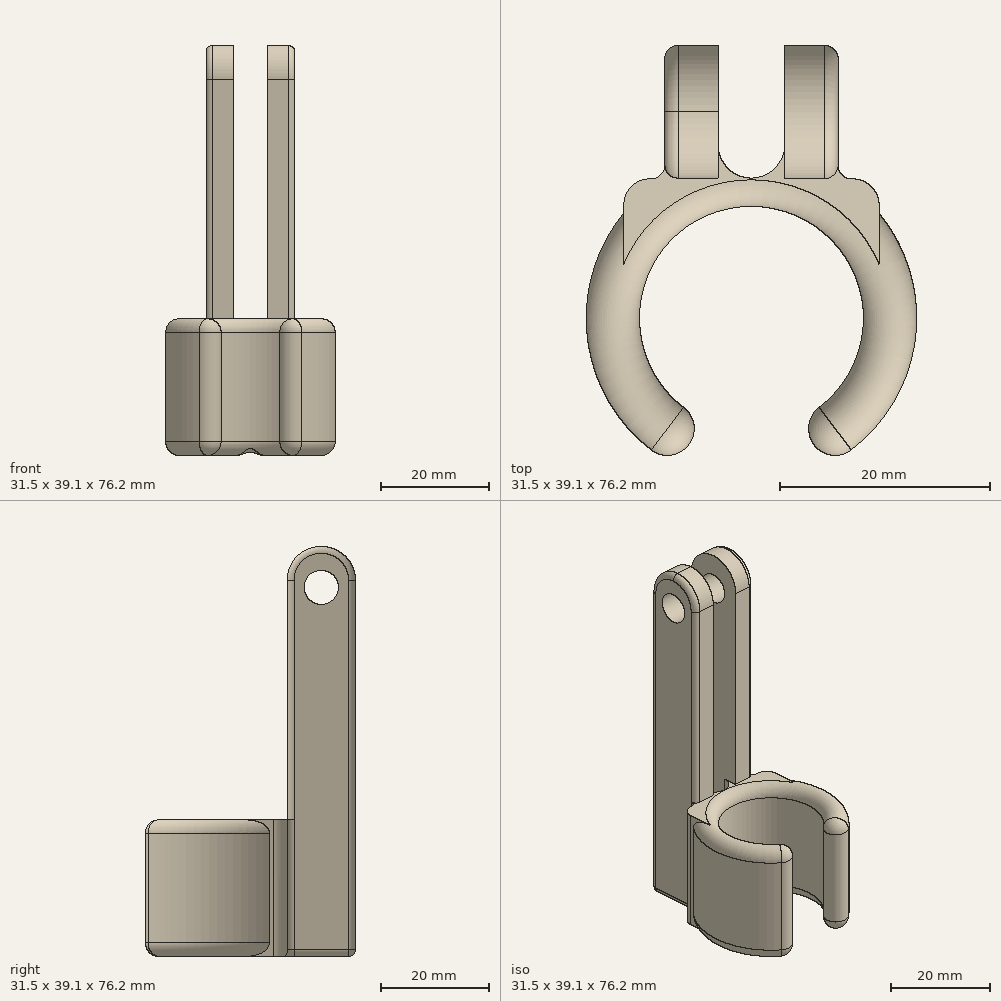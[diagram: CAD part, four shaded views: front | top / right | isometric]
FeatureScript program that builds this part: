
annotation { "Feature Type Name" : "Feature", "Feature Type Description" : "" }
export const myFeature = defineFeature(function(context is Context, id is Id, definition is map)
    precondition{}
    {
        {
            var Q0;
            Q0=qCreatedBy(makeId("Top.planeOp"),FACE);
            var sketch = newSketch(context, id + "F0", { "sketchPlane" : qUnion([Q0])});
            skArc(sketch, "E0", {"start": v(5.08, -9.38) * mm, "mid": v(0, 10.67) * mm, "end": v(-5.08, -9.38) * mm});
            skArc(sketch, "E1", {"start": v(6.35, -14.41) * mm, "mid": v(15.32, -3.65) * mm, "end": v(12.16, 10) * mm});
            skLineSegment(sketch, "E2", {"start": v(-5.08, -9.38) * mm, "end": v(-6.35, -14.41) * mm});
            skLineSegment(sketch, "E3", {"start": v(5.08, -9.38) * mm, "end": v(6.35, -14.41) * mm});
            skLineSegment(sketch, "E4", {"start": v(-12.16, 10) * mm, "end": v(-12.16, 13.3) * mm});
            skLineSegment(sketch, "E5", {"start": v(12.16, 13.3) * mm, "end": v(12.16, 10) * mm});
            skArc(sketch, "E6.trimOffspring", {"start": v(-12.16, 10) * mm, "mid": v(-15.32, -3.65) * mm, "end": v(-6.35, -14.41) * mm});
            skLineSegment(sketch, "E7", {"start": v(0, 0) * mm, "end": v(0, 28.54) * mm, "construction": true});
            skPoint(sketch, "E7.endSnap0", {"position": v(0, 28.54) * mm});
            skLineSegment(sketch, "E8.trimOffspring", {"start": v(8.26, 13.3) * mm, "end": v(12.16, 13.3) * mm});
            skLineSegment(sketch, "E9.trimOffspring", {"start": v(-12.16, 13.3) * mm, "end": v(-8.26, 13.3) * mm});
            skLineSegment(sketch, "E10", {"start": v(-8.26, 13.3) * mm, "end": v(-8.26, 26) * mm});
            skLineSegment(sketch, "E11", {"start": v(-8.26, 26) * mm, "end": v(-3.17, 26) * mm});
            skLineSegment(sketch, "E12", {"start": v(-3.17, 26) * mm, "end": v(-3.18, 13.37) * mm});
            skLineSegment(sketch, "E13", {"start": v(-3.18, 13.37) * mm, "end": v(0, 13.37) * mm});
            skLineSegment(sketch, "E14", {"start": v(0, 13.37) * mm, "end": v(3.18, 13.37) * mm});
            skLineSegment(sketch, "E15", {"start": v(3.18, 13.37) * mm, "end": v(3.18, 26) * mm});
            skLineSegment(sketch, "E16", {"start": v(3.17, 26) * mm, "end": v(8.26, 26) * mm});
            skLineSegment(sketch, "E17", {"start": v(8.26, 26) * mm, "end": v(8.26, 13.3) * mm});
            skSolve(sketch);
        }
        {
            var Q0;
            Q0=qSketchRegion(id+"F0",true);
            extrude(context, id + "F1", {"entities" : qUnion([Q0]), "depth" : 25.4 * mm, "offsetDistance" : 25.4 * mm});
        }
        {
            var Q0;
            Q0=makeQuery(id+"F1.opExtrude","SWEPT_EDGE",EDGE,{"disambiguationData":[OSD([sQuery(id+"F0.wireOp",EDGE,"E0"),sQuery(id+"F0.wireOp",EDGE,"E3")])]});
            var Q1;
            Q1=makeQuery(id+"F1.opExtrude","SWEPT_EDGE",EDGE,{"disambiguationData":[OSD([sQuery(id+"F0.wireOp",EDGE,"E0"),sQuery(id+"F0.wireOp",EDGE,"E2")])]});
            var Q2;
            Q2=makeQuery(id+"F1.opExtrude","SWEPT_EDGE",EDGE,{"disambiguationData":[OSD([sQuery(id+"F0.wireOp",EDGE,"E1"),sQuery(id+"F0.wireOp",EDGE,"E3")])]});
            var Q3;
            Q3=makeQuery(id+"F1.opExtrude","SWEPT_EDGE",EDGE,{"disambiguationData":[OSD([sQuery(id+"F0.wireOp",EDGE,"E2"),sQuery(id+"F0.wireOp",EDGE,"E6.trimOffspring")])]});
            fillet(context, id + "F2", {"entities" : qUnion([Q0, Q1, Q2, Q3]), "radius" : 2.54 * mm, "tangentPropagation" : true, "allowEdgeOverflow" : false});
        }
        {
            var Q0;
            Q0=makeQuery(id+"F1.opExtrude","CAP_FACE",FACE,{"disambiguationData":[OSD([sQuery(id+"F0.wireOp",EDGE,"E0"),sQuery(id+"F0.wireOp",EDGE,"E1"),sQuery(id+"F0.wireOp",EDGE,"E2"),sQuery(id+"F0.wireOp",EDGE,"E3"),sQuery(id+"F0.wireOp",EDGE,"E4"),sQuery(id+"F0.wireOp",EDGE,"E5"),sQuery(id+"F0.wireOp",EDGE,"E6.trimOffspring"),sQuery(id+"F0.wireOp",EDGE,"E8.trimOffspring"),sQuery(id+"F0.wireOp",EDGE,"E9.trimOffspring"),sQuery(id+"F0.wireOp",EDGE,"E10"),sQuery(id+"F0.wireOp",EDGE,"E11"),sQuery(id+"F0.wireOp",EDGE,"E12"),sQuery(id+"F0.wireOp",EDGE,"E13"),sQuery(id+"F0.wireOp",EDGE,"E14"),sQuery(id+"F0.wireOp",EDGE,"E15"),sQuery(id+"F0.wireOp",EDGE,"E16"),sQuery(id+"F0.wireOp",EDGE,"E17")])],"isStart":false});
            var sketch = newSketch(context, id + "F3", { "sketchPlane" : qUnion([Q0])});
            skLineSegment(sketch, "E18.bottom", {"start": v(-8.26, 26) * mm, "end": v(-3.18, 26) * mm});
            skLineSegment(sketch, "E18.top", {"start": v(-8.26, 13.37) * mm, "end": v(-3.18, 13.37) * mm});
            skLineSegment(sketch, "E18.left", {"start": v(-8.26, 26) * mm, "end": v(-8.26, 13.37) * mm});
            skLineSegment(sketch, "E18.right", {"start": v(-3.18, 26) * mm, "end": v(-3.18, 13.37) * mm});
            skLineSegment(sketch, "E19.bottom", {"start": v(3.18, 26) * mm, "end": v(8.26, 26) * mm});
            skLineSegment(sketch, "E19.top", {"start": v(3.18, 13.3) * mm, "end": v(8.26, 13.3) * mm});
            skLineSegment(sketch, "E19.left", {"start": v(3.18, 26) * mm, "end": v(3.18, 13.3) * mm});
            skLineSegment(sketch, "E19.right", {"start": v(8.26, 26) * mm, "end": v(8.26, 13.3) * mm});
            skSolve(sketch);
        }
        {
            var Q0;
            Q0 = qSketchRegion(id + "F3", true);
            extrude(context, id + "F4", {"entities" : qUnion([Q0]), "operationType" : NewBodyOperationType.ADD, "depth" : 50.8 * mm, "offsetDistance" : 25.4 * mm});
        }
        {
            var Q0;
            Q0=makeQuery(id+"F4.opExtrude","CAP_EDGE",EDGE,{"disambiguationData":[OSD([sQuery(id+"F3.wireOp",EDGE,"E18.top")])],"isStart":false});
            var Q1;
            Q1=makeQuery(id+"F4.opExtrude","CAP_EDGE",EDGE,{"disambiguationData":[OSD([sQuery(id+"F3.wireOp",EDGE,"E18.bottom")])],"isStart":false});
            var Q2;
            Q2=makeQuery(id+"F4.opExtrude","CAP_EDGE",EDGE,{"disambiguationData":[OSD([sQuery(id+"F3.wireOp",EDGE,"E19.bottom")])],"isStart":false});
            var Q3;
            Q3=makeQuery(id+"F4.opExtrude","CAP_EDGE",EDGE,{"disambiguationData":[OSD([sQuery(id+"F3.wireOp",EDGE,"E19.top")])],"isStart":false});
            fillet(context, id + "F5", {"entities" : qUnion([Q0, Q1, Q2, Q3]), "radius" : 6.35 * mm, "tangentPropagation" : true, "allowEdgeOverflow" : false});
        }
        {
            var Q0;
            Q0=makeQuery(id+"F1.opExtrude","SWEPT_EDGE",EDGE,{"disambiguationData":[OSD([sQuery(id+"F0.wireOp",EDGE,"E12"),sQuery(id+"F0.wireOp",EDGE,"E13")])]});
            var Q1;
            Q1=makeQuery(id+"F1.opExtrude","SWEPT_EDGE",EDGE,{"disambiguationData":[OSD([sQuery(id+"F0.wireOp",EDGE,"E14"),sQuery(id+"F0.wireOp",EDGE,"E15")])]});
            fillet(context, id + "F6", {"entities" : qUnion([Q0, Q1]), "radius" : 3.17 * mm, "tangentPropagation" : true, "allowEdgeOverflow" : false});
        }
        {
            var Q0;
            Q0=makeQuery(id+"F1.opExtrude","SWEPT_EDGE",EDGE,{"disambiguationData":[OSD([sQuery(id+"F0.wireOp",EDGE,"E4"),sQuery(id+"F0.wireOp",EDGE,"E9.trimOffspring")])]});
            var Q1;
            Q1=makeQuery(id+"F1.opExtrude","CAP_EDGE",EDGE,{"disambiguationData":[OSD([sQuery(id+"F0.wireOp",EDGE,"E6.trimOffspring")])],"isStart":true});
            var Q2;
            Q2=makeQuery(id+"F1.opExtrude","SWEPT_EDGE",EDGE,{"disambiguationData":[OSD([sQuery(id+"F0.wireOp",EDGE,"E5"),sQuery(id+"F0.wireOp",EDGE,"E8.trimOffspring")])]});
            var Q3;
            Q3=makeQuery(id+"F1.opExtrude","CAP_EDGE",EDGE,{"disambiguationData":[OSD([sQuery(id+"F0.wireOp",EDGE,"E0")])],"isStart":false});
            fillet(context, id + "F7", {"entities" : qUnion([Q0, Q1, Q2, Q3]), "radius" : 2.54 * mm, "tangentPropagation" : true, "allowEdgeOverflow" : false});
        }
        {
            var Q0;
            Q0=makeQuery(id+"F4.boolean.opBoolean","MERGE",EDGE,{"derivedFrom":[makeQuery(id+"F1.opExtrude","SWEPT_EDGE",EDGE,{"disambiguationData":[OSD([sQuery(id+"F0.wireOp",EDGE,"E16"),sQuery(id+"F0.wireOp",EDGE,"E17")])]}),makeQuery(id+"F4.opExtrude","SWEPT_EDGE",EDGE,{"disambiguationData":[OSD([sQuery(id+"F3.wireOp",EDGE,"E19.bottom"),sQuery(id+"F3.wireOp",EDGE,"E19.right")])]})]});
            var Q1;
            Q1=makeQuery(id+"F4.boolean.opBoolean","MERGE",EDGE,{"derivedFrom":[makeQuery(id+"F1.opExtrude","SWEPT_EDGE",EDGE,{"disambiguationData":[OSD([sQuery(id+"F0.wireOp",EDGE,"E10"),sQuery(id+"F0.wireOp",EDGE,"E11")])]}),makeQuery(id+"F4.opExtrude","SWEPT_EDGE",EDGE,{"disambiguationData":[OSD([sQuery(id+"F3.wireOp",EDGE,"E18.bottom"),sQuery(id+"F3.wireOp",EDGE,"E18.left")])]})]});
            var Q2;
            Q2=makeQuery(id+"F4.opExtrude","SWEPT_EDGE",EDGE,{"disambiguationData":[OSD([sQuery(id+"F0.wireOp",EDGE,"E10"),sQuery(id+"F3.wireOp",EDGE,"E18.top"),sQuery(id+"F3.wireOp",EDGE,"E18.left")])]});
            fillet(context, id + "F8", {"entities" : qUnion([Q0, Q1, Q2]), "radius" : 1.27 * mm, "tangentPropagation" : true, "allowEdgeOverflow" : false});
        }
        {
            var Q0;
            Q0=makeQuery(id+"F4.boolean.opBoolean","MERGE",FACE,{"derivedFrom":[makeQuery(id+"F1.opExtrude","SWEPT_FACE",FACE,{"disambiguationData":[OSD([sQuery(id+"F0.wireOp",EDGE,"E17")])]}),makeQuery(id+"F4.opExtrude","SWEPT_FACE",FACE,{"disambiguationData":[OSD([sQuery(id+"F3.wireOp",EDGE,"E19.right")])]})]});
            var sketch = newSketch(context, id + "F9", { "sketchPlane" : qUnion([Q0])});
            skCircle(sketch, "E20", {"center": v(19.65, 68.58) * mm, "radius": 3.18 * mm});
            skSolve(sketch);
        }
        {
            var Q0;
            Q0 = qSketchRegion(id + "F9", true);
            extrude(context, id + "F10", {"entities" : qUnion([Q0]), "operationType" : NewBodyOperationType.REMOVE, "endBound" : BoundingType.THROUGH_ALL, "oppositeDirection" : true, "depth" : 25.4 * mm, "offsetDistance" : 25.4 * mm});
        }
        {
            var Q0;
            Q0=makeQuery(id+"F1.opExtrude","CAP_EDGE",EDGE,{"disambiguationData":[OSD([sQuery(id+"F0.wireOp",EDGE,"E10")])],"isStart":true});
            var Q1;
            Q1=makeQuery(id+"F1.opExtrude","CAP_EDGE",EDGE,{"disambiguationData":[OSD([sQuery(id+"F0.wireOp",EDGE,"E15")])],"isStart":true});
            var Q2;
            Q2=makeQuery(id+"F1.opExtrude","CAP_EDGE",EDGE,{"disambiguationData":[OSD([sQuery(id+"F0.wireOp",EDGE,"E17")])],"isStart":true});
            var Q3;
            Q3=makeQuery(id+"F1.opExtrude","SWEPT_EDGE",EDGE,{"disambiguationData":[OSD([sQuery(id+"F0.wireOp",EDGE,"E8.trimOffspring"),sQuery(id+"F0.wireOp",EDGE,"E17")])]});
            var Q4;
            Q4=makeQuery(id+"F1.opExtrude","SWEPT_EDGE",EDGE,{"disambiguationData":[OSD([sQuery(id+"F0.wireOp",EDGE,"E9.trimOffspring"),sQuery(id+"F0.wireOp",EDGE,"E10")])]});
            fillet(context, id + "F11", {"entities" : qUnion([Q0, Q1, Q2, Q3, Q4]), "radius" : 1.27 * mm, "tangentPropagation" : true, "allowEdgeOverflow" : false});
        }
    });
